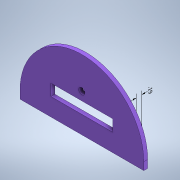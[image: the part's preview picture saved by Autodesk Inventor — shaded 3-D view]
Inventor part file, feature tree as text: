
AUTODESK INVENTOR PART (.ipt)
format: ipt  version: 2021.1 (Build 251245000, 245)  size: 161,280 bytes
history: native  units: in
note: dims shown in document units (in); Inventor stores cm internally (conversion verified against a paired STEP export)
features: sketch x3, extrude x3, other x2, hole x1
ambient origin geometry x8: Origin, YZ Plane, XZ Plane, XY Plane, X Axis, Y Axis, Z Axis, Center Point
bodies: Solid2 (feature_tree)
feature tree (9):
  other  "Annotations"
  sketch  "Sketch2"  dims[d2=2.5in d3=0.375in]
  extrude  "Extrusion3"  Depth=0.375in
  extrude  "Extrusion4"  Depth=1.0in
  hole  "Hole2"  [1 undecoded]
  extrude  "Extrusion6"  Depth=0.125in TaperAngle=0.0deg
  sketch  "Sketch5"  dims[d4=0.375in d5=1.0in]
  sketch  "Sketch8"  dims[d6=0.325in d7=0.375in d12=0.125in d13=0.0in d14=0.1875in d15=0.0in d23=0.201in d24=0.75in d25=0.375in d26=0.19in d27=0.5635in d28=1.0in d29=0.8108in d32=0.25in d33=0.0in d34=0.1875in]
  other  "Linear Dimension 1"
note: 1 required parameter value undecoded (feature->parameter linkage not recoverable at this tier; creation-order binding heuristic only, values carry confidence <= 0.55)
